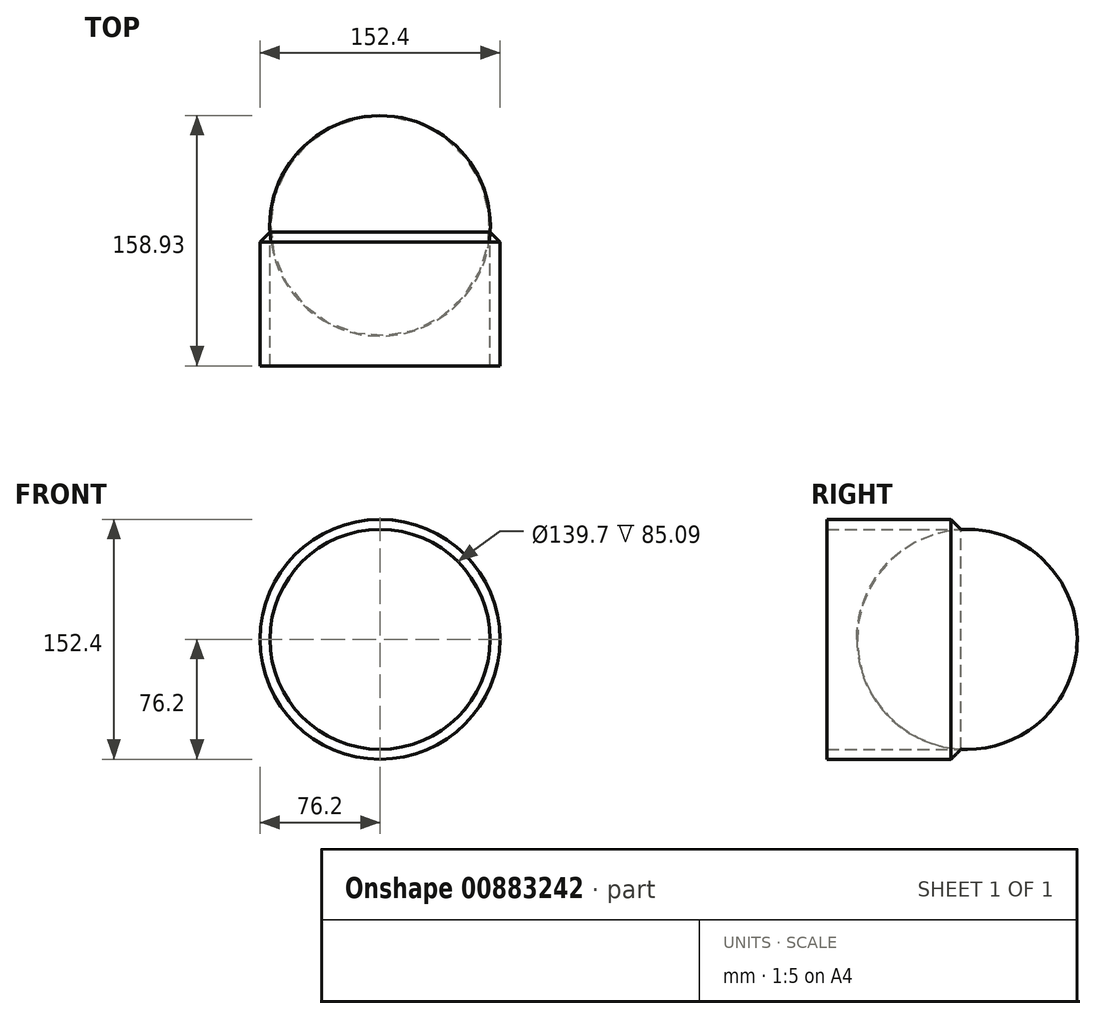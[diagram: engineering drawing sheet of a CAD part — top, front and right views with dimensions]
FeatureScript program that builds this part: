
annotation { "Feature Type Name" : "Feature", "Feature Type Description" : "" }
export const myFeature = defineFeature(function(context is Context, id is Id, definition is map)
    precondition{}
    {
        {
            var Q0;
            Q0=qCreatedBy(makeId("Front.planeOp"),FACE);
            var sketch = newSketch(context, id + "F0", { "sketchPlane" : qUnion([Q0])});
            skCircle(sketch, "E0", {"center": v(0, 0) * mm, "radius": 76.2 * mm});
            skCircle(sketch, "E1", {"center": v(0, 0) * mm, "radius": 69.85 * mm});
            skSolve(sketch);
        }
        {
            var Q0;
            Q0=makeQuery(id+"F0.imprint","IMPRINT",FACE,{"disambiguationData":[TD([[makeQuery(id+"F0.imprint","IMPRINT",EDGE,{"derivedFrom":sQuery(id+"F0.wireOp",EDGE,"E0")}),1.0]])]});
            extrude(context, id + "F1", {"entities" : qUnion([Q0]), "depth" : 88.9 * mm, "offsetDistance" : 25.4 * mm});
        }
        {
            var Q0;
            Q0=qCreatedBy(makeId("Front.planeOp"),FACE);
            var sketch = newSketch(context, id + "F2", { "sketchPlane" : qUnion([Q0])});
            skArc(sketch, "E2", {"start": v(0, 69.85) * mm, "mid": v(-69.67, 0) * mm, "end": v(0, -69.85) * mm});
            skLineSegment(sketch, "E3", {"start": v(0, 69.85) * mm, "end": v(0, -69.85) * mm});
            skLineSegment(sketch, "E4", {"start": v(0, 69.85) * mm, "end": v(0, -69.85) * mm, "construction": true});
            skSolve(sketch);
        }
        {
            var Q0;
            Q0 = qSketchRegion(id + "F2", true);
            var Q1;
            Q1=sQuery(id+"F2.wireOp",EDGE,"E3");
            revolve(context, id + "F3", {"surfaceOperationType" : NewSurfaceOperationType.NEW, "entities" : qUnion([Q0]), "axis" : qUnion([Q1]), "revolveType" : RevolveType.FULL});
        }
        {
            var Q0;
            Q0=makeQuery(id+"F1.opExtrude","CAP_EDGE",EDGE,{"disambiguationData":[OSD([sQuery(id+"F0.wireOp",EDGE,"E0")])],"isStart":true});
            chamfer(context, id + "F4", {"entities" : qUnion([Q0]), "width" : 10.16 * mm, "tangentPropagation" : true});
        }
    });
